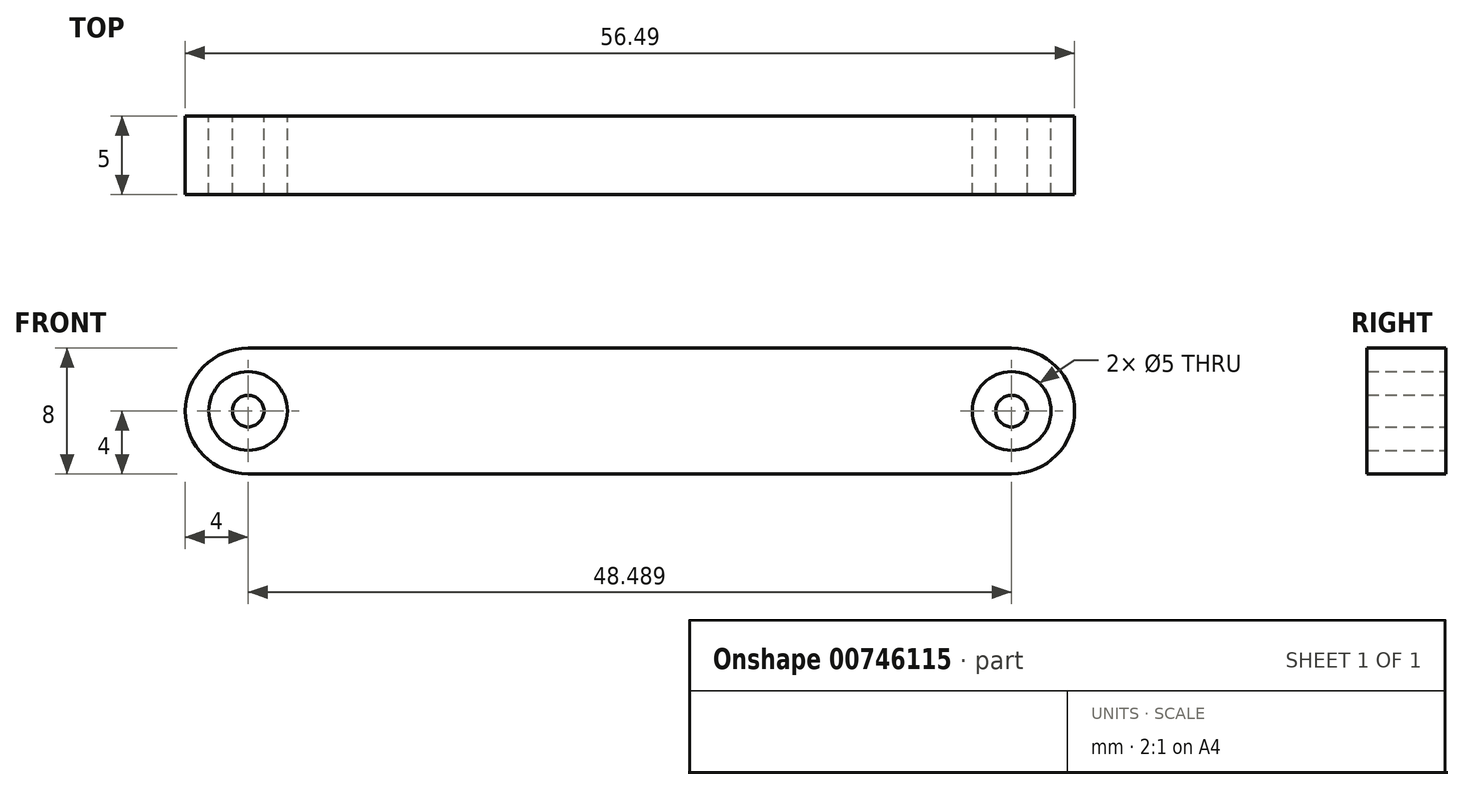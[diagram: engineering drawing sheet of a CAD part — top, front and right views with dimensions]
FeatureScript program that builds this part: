
annotation { "Feature Type Name" : "Feature", "Feature Type Description" : "" }
export const myFeature = defineFeature(function(context is Context, id is Id, definition is map)
    precondition{}
    {
        {
            var Q0;
            Q0=qCreatedBy(makeId("Front.planeOp"),FACE);
            var sketch = newSketch(context, id + "F0", { "sketchPlane" : qUnion([Q0])});
            skArc(sketch, "E0", {"start": v(0, 4) * mm, "mid": v(-4, 0) * mm, "end": v(0, -4) * mm});
            skCircle(sketch, "E1", {"center": v(0, 0) * mm, "radius": 2.5 * mm});
            skCircle(sketch, "E2", {"center": v(0, 0) * mm, "radius": 1 * mm});
            skArc(sketch, "E3", {"start": v(48.49, -4) * mm, "mid": v(52.49, 0) * mm, "end": v(48.49, 4) * mm});
            skCircle(sketch, "E4", {"center": v(48.49, 0) * mm, "radius": 2.5 * mm});
            skCircle(sketch, "E5", {"center": v(48.49, 0) * mm, "radius": 1 * mm});
            skLineSegment(sketch, "E6", {"start": v(0, 4) * mm, "end": v(48.49, 4) * mm});
            skLineSegment(sketch, "E7", {"start": v(0, -4) * mm, "end": v(48.49, -4) * mm});
            skSolve(sketch);
        }
        {
            var Q0;
            Q0=makeQuery(id+"F0.imprint","IMPRINT",FACE,{"disambiguationData":[TD([[makeQuery(id+"F0.imprint","IMPRINT",EDGE,{"derivedFrom":sQuery(id+"F0.wireOp",EDGE,"E0")}),1.0]])]});
            var Q1;
            Q1=makeQuery(id+"F0.imprint","IMPRINT",FACE,{"disambiguationData":[TD([[makeQuery(id+"F0.imprint","IMPRINT",EDGE,{"derivedFrom":sQuery(id+"F0.wireOp",EDGE,"E2")}),1.0]])]});
            var Q2;
            Q2=makeQuery(id+"F0.imprint","IMPRINT",FACE,{"disambiguationData":[TD([[makeQuery(id+"F0.imprint","IMPRINT",EDGE,{"derivedFrom":sQuery(id+"F0.wireOp",EDGE,"E5")}),1.0]])]});
            extrude(context, id + "F1", {"entities" : qUnion([Q0, Q1, Q2]), "depth" : 5 * mm, "offsetDistance" : 25.4 * mm});
        }
    });
